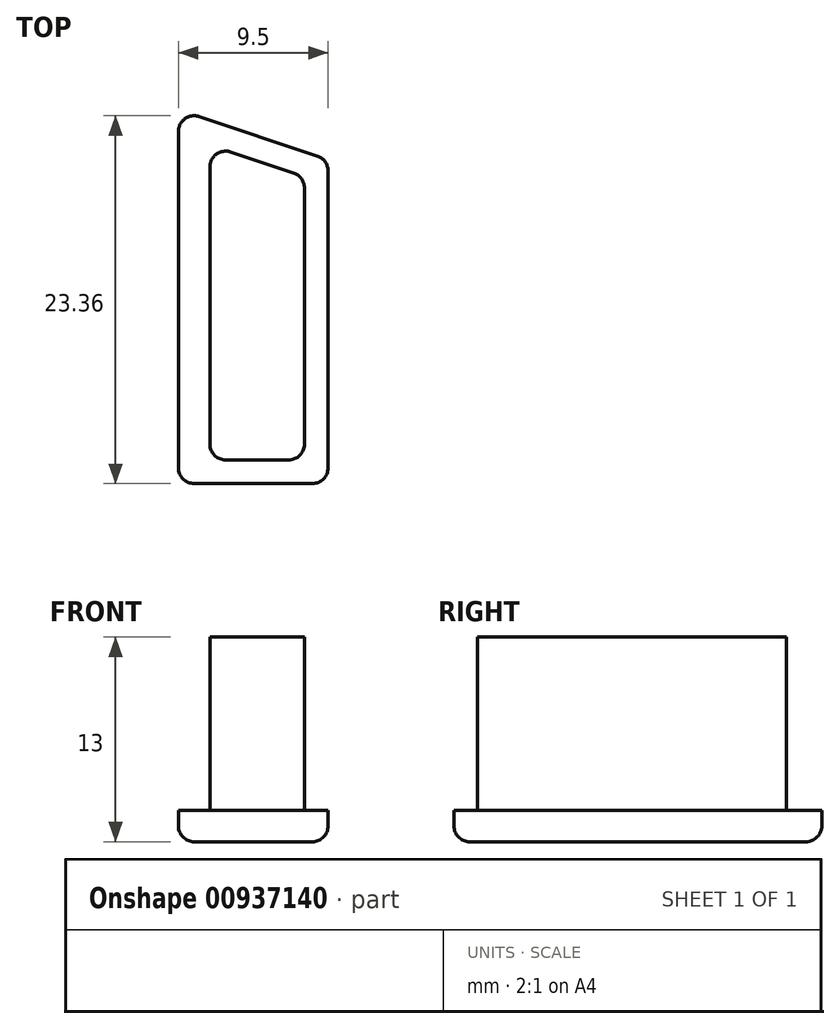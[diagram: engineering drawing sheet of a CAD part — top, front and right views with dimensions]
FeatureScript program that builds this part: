
annotation { "Feature Type Name" : "Feature", "Feature Type Description" : "" }
export const myFeature = defineFeature(function(context is Context, id is Id, definition is map)
    precondition{}
    {
        {
            var Q0;
            Q0=qCreatedBy(makeId("Top.planeOp"),FACE);
            var sketch = newSketch(context, id + "F0", { "sketchPlane" : qUnion([Q0])});
            skLineSegment(sketch, "E0", {"start": v(0, 20.58) * mm, "end": v(0, 0) * mm});
            skLineSegment(sketch, "E1.MirrorCS", {"start": v(0, 0) * mm, "end": v(-9.5, 0) * mm});
            skLineSegment(sketch, "E2.MirrorCS", {"start": v(-7.5, 1.5) * mm, "end": v(-7.5, 21.5) * mm});
            skLineSegment(sketch, "E3.MirrorCS", {"start": v(-1.5, 1.5) * mm, "end": v(-7.5, 1.5) * mm});
            skLineSegment(sketch, "E4.MirrorCS", {"start": v(-9.5, 23.75) * mm, "end": v(0, 20.58) * mm});
            skLineSegment(sketch, "E5.MirrorCS", {"start": v(-9.5, 0) * mm, "end": v(-9.5, 23.75) * mm});
            skLineSegment(sketch, "E6.MirrorCS", {"start": v(-7.5, 21.5) * mm, "end": v(-1.5, 19.5) * mm});
            skLineSegment(sketch, "E7.MirrorCS", {"start": v(-1.5, 19.5) * mm, "end": v(-1.5, 1.5) * mm});
            skSolve(sketch);
        }
        {
            var Q0;
            Q0=makeQuery(id+"F0.imprint","IMPRINT",FACE,{"disambiguationData":[TD([[makeQuery(id+"F0.imprint","IMPRINT",EDGE,{"derivedFrom":sQuery(id+"F0.wireOp",EDGE,"E1.MirrorCS")}),-1.0]])]});
            var Q1;
            Q1=makeQuery(id+"F0.imprint","IMPRINT",FACE,{"disambiguationData":[TD([[makeQuery(id+"F0.imprint","IMPRINT",EDGE,{"derivedFrom":sQuery(id+"F0.wireOp",EDGE,"E2.MirrorCS")}),-1.0]])]});
            extrude(context, id + "F1", {"entities" : qUnion([Q0, Q1]), "depth" : 2 * mm, "offsetDistance" : 25 * mm});
        }
        {
            var Q0;
            Q0=makeQuery(id+"F0.imprint","IMPRINT",FACE,{"disambiguationData":[TD([[makeQuery(id+"F0.imprint","IMPRINT",EDGE,{"derivedFrom":sQuery(id+"F0.wireOp",EDGE,"E2.MirrorCS")}),-1.0]])]});
            extrude(context, id + "F2", {"entities" : qUnion([Q0]), "operationType" : NewBodyOperationType.ADD, "depth" : 13 * mm, "offsetDistance" : 25 * mm});
        }
        {
            var Q0;
            Q0=makeQuery(id+"F2.opExtrude","SWEPT_EDGE",EDGE,{"disambiguationData":[OSD([sQuery(id+"F0.wireOp",EDGE,"E2.MirrorCS"),sQuery(id+"F0.wireOp",EDGE,"E6.MirrorCS")])]});
            var Q1;
            Q1=makeQuery(id+"F1.opExtrude","SWEPT_EDGE",EDGE,{"disambiguationData":[OSD([sQuery(id+"F0.wireOp",EDGE,"E4.MirrorCS"),sQuery(id+"F0.wireOp",EDGE,"E5.MirrorCS")])]});
            var Q2;
            Q2=makeQuery(id+"F1.opExtrude","SWEPT_EDGE",EDGE,{"disambiguationData":[OSD([sQuery(id+"F0.wireOp",EDGE,"E0"),sQuery(id+"F0.wireOp",EDGE,"E4.MirrorCS")])]});
            var Q3;
            Q3=makeQuery(id+"F2.opExtrude","SWEPT_EDGE",EDGE,{"disambiguationData":[OSD([sQuery(id+"F0.wireOp",EDGE,"E6.MirrorCS"),sQuery(id+"F0.wireOp",EDGE,"E7.MirrorCS")])]});
            var Q4;
            Q4=makeQuery(id+"F1.opExtrude","SWEPT_EDGE",EDGE,{"disambiguationData":[OSD([sQuery(id+"F0.wireOp",EDGE,"E1.MirrorCS"),sQuery(id+"F0.wireOp",EDGE,"E0")])]});
            var Q5;
            Q5=makeQuery(id+"F2.opExtrude","SWEPT_EDGE",EDGE,{"disambiguationData":[OSD([sQuery(id+"F0.wireOp",EDGE,"E3.MirrorCS"),sQuery(id+"F0.wireOp",EDGE,"E7.MirrorCS")])]});
            var Q6;
            Q6=makeQuery(id+"F1.opExtrude","SWEPT_EDGE",EDGE,{"disambiguationData":[OSD([sQuery(id+"F0.wireOp",EDGE,"E1.MirrorCS"),sQuery(id+"F0.wireOp",EDGE,"E5.MirrorCS")])]});
            var Q7;
            Q7=makeQuery(id+"F2.opExtrude","SWEPT_EDGE",EDGE,{"disambiguationData":[OSD([sQuery(id+"F0.wireOp",EDGE,"E2.MirrorCS"),sQuery(id+"F0.wireOp",EDGE,"E3.MirrorCS")])]});
            var Q8;
            Q8=makeQuery(id+"F1.opExtrude","CAP_EDGE",EDGE,{"disambiguationData":[OSD([sQuery(id+"F0.wireOp",EDGE,"E5.MirrorCS")])],"isStart":true});
            var Q9;
            Q9=makeQuery(id+"F1.opExtrude","CAP_EDGE",EDGE,{"disambiguationData":[OSD([sQuery(id+"F0.wireOp",EDGE,"E1.MirrorCS")])],"isStart":true});
            var Q10;
            Q10=makeQuery(id+"F1.opExtrude","CAP_EDGE",EDGE,{"disambiguationData":[OSD([sQuery(id+"F0.wireOp",EDGE,"E4.MirrorCS")])],"isStart":true});
            var Q11;
            Q11=makeQuery(id+"F1.opExtrude","CAP_EDGE",EDGE,{"disambiguationData":[OSD([sQuery(id+"F0.wireOp",EDGE,"E0")])],"isStart":true});
            fillet(context, id + "F3", {"entities" : qUnion([Q0, Q1, Q2, Q3, Q4, Q5, Q6, Q7, Q8, Q9, Q10, Q11]), "radius" : 1 * mm, "tangentPropagation" : true, "allowEdgeOverflow" : false});
        }
    });
